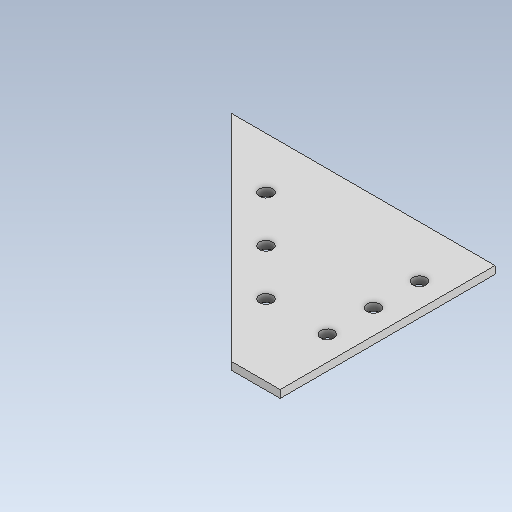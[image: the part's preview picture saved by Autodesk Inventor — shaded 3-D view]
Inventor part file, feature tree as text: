
AUTODESK INVENTOR PART (.ipt)
format: ipt  version: 2023 (Build 270158000, 158)  size: 98,304 bytes
history: native  units: in
note: dims shown in document units (in); Inventor stores cm internally (conversion verified against a paired STEP export)
features: other x3, sketch x1
ambient origin geometry x8: Origin, YZ Plane, XZ Plane, XY Plane, X Axis, Y Axis, Z Axis, Center Point
bodies: Solid1 (feature_tree)
feature tree (4):
  other  "CH-1-01-FrontKneeJoint.ipt"
  other  "Solid1::CH-1-01-FrontKneeJoint.ipt"
  other  "TaggingFeature1"
  sketch  "Sketch1"  dims[d0=0.3937in]
